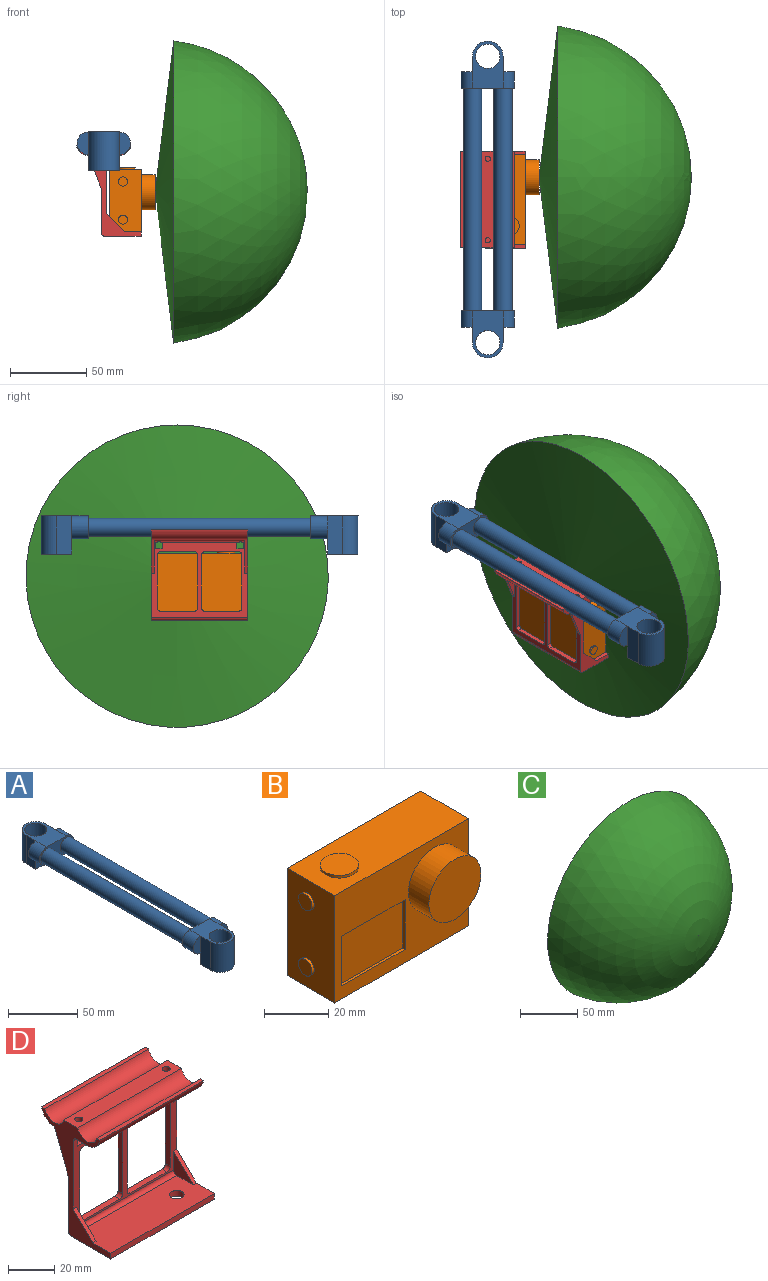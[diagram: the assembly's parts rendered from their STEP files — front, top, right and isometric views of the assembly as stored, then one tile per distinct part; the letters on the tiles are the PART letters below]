
ASSEMBLY  parts=4 mates=3
PART A: 28 faces, bbox 35x208x25 mm
  f0: plane 15x7.5mm, normal (0,1,0), area 88.4mm2, adj f11,f23
  f1: plane 15x7.5mm, normal (0,-1,0), area 88.4mm2, adj f7,f20
  f2: cylinder r=7.5mm len=15mm, axis (0,1,0), area 259.2mm2, adj f3,f4,f5,f6
  f3: plane 31x20mm, normal (0,0,1), area 376mm2, adj f2,f5,f7,f17,f18,f19,f20
  f4: plane 20x11mm, normal (0,0,-1), area 220mm2, adj f2,f5,f7,f16
  f5: plane 35x15mm, normal (0,1,0), area 250.5mm2, adj f2,f3,f4,f7,f8,f9
  f6: plane 15x7.5mm, normal (0,-1,0), area 88.4mm2, adj f2,f17
  f7: cylinder r=7.5mm len=15mm, axis (0,1,0), area 259.2mm2, adj f1,f3,f4,f5
  f8: cylinder r=6mm len=146mm, axis (0,1,0), area 5504.1mm2, adj f5,f10
  f9: cylinder r=6mm len=146mm, axis (0,1,0), area 5504.1mm2, adj f5,f10
  f10: plane 35x15mm, normal (0,-1,0), area 250.5mm2, adj f8,f9,f11,f12,f13,f14
  f11: cylinder r=7.5mm len=15mm, axis (0,-1,0), area 259.2mm2, adj f0,f10,f12,f13
  f12: plane 20x11mm, normal (0,0,-1), area 220mm2, adj f10,f11,f14,f22
  f13: plane 31x20mm, normal (0,0,1), area 376mm2, adj f10,f11,f14,f23,f24,f25,f26
  f14: cylinder r=7.5mm len=15mm, axis (0,-1,0), area 259.2mm2, adj f10,f12,f13,f15
  f15: plane 15x7.5mm, normal (0,1,0), area 88.4mm2, adj f14,f26
  f16: plane 20x10mm, normal (0,1,0), area 200mm2, adj f4,f17,f20,f21
  f17: plane 25x10mm, normal (-1,0,0), area 250mm2, adj f3,f6,f16,f18,f21
  f18: cylinder r=10mm len=25mm, axis (0,0,1), area 785.4mm2, adj f3,f17,f20,f21
  f19: cylinder r=8mm len=25mm, axis (0,0,1), area 1256.6mm2, adj f3,f21
  f20: plane 25x10mm, normal (1,0,0), area 250mm2, adj f1,f3,f16,f18,f21
  f21: plane 20x20mm, normal (0,0,-1), area 156mm2, adj f16,f17,f18,f19,f20
  f22: plane 20x10mm, normal (0,-1,0), area 200mm2, adj f12,f23,f26,f27
  f23: plane 25x10mm, normal (-1,0,0), area 250mm2, adj f0,f13,f22,f24,f27
  f24: cylinder r=10mm len=25mm, axis (0,0,1), area 785.4mm2, adj f13,f23,f26,f27
  f25: cylinder r=8mm len=25mm, axis (0,0,1), area 1256.6mm2, adj f13,f27
  f26: plane 25x10mm, normal (1,0,0), area 250mm2, adj f13,f15,f22,f24,f27
  f27: plane 20x20mm, normal (0,0,-1), area 156mm2, adj f22,f23,f24,f25,f26
PART B: 26 faces, bbox 60x30.1x42 mm
  f0: plane 41x21.1mm, normal (-1,0,0), area 808.6mm2, adj f1,f2,f3,f4,f5,f6
  f1: plane 59x21.1mm, normal (0,0,-1), area 1213.2mm2, adj f0,f2,f3,f7,f8
  f2: plane 59x41mm, normal (0,1,0), area 2419mm2, adj f0,f1,f4,f7
  f3: plane 59x41mm, normal (0,-1,0), area 1471.5mm2, adj f0,f1,f4,f7,f9,f10,f11,f12
  f4: plane 59x21.1mm, normal (0,0,1), area 1131.8mm2, adj f0,f2,f3,f7,f14
  f5: cylinder r=3mm len=6mm, axis (1,0,0), area 18.8mm2, adj f0,f15
  f6: cylinder r=3mm len=6mm, axis (1,0,0), area 18.8mm2, adj f0,f16
  f7: plane 41x21.1mm, normal (1,0,0), area 645.1mm2, adj f1,f2,f3,f4,f17,f18,f19,f20
  f8: cylinder r=3.17mm len=6.35mm, axis (0,0,-1), area 99.7mm2, adj f1,f21
  f9: plane 28x1mm, normal (0,0,-1), area 28mm2, adj f3,f10,f12,f22
  f10: plane 19x1mm, normal (1,0,0), area 19mm2, adj f3,f9,f11,f22
  f11: plane 28x1mm, normal (0,0,1), area 28mm2, adj f3,f10,f12,f22
  f12: plane 19x1mm, normal (-1,0,0), area 19mm2, adj f3,f9,f11,f22
  f13: cylinder r=11.5mm len=23mm, axis (0,1,0), area 650.3mm2, adj f3,f23
  f14: cylinder r=6mm len=12mm, axis (0,0,-1), area 37.7mm2, adj f4,f24
  f15: plane 6x6mm, normal (-1,0,0), area 28.3mm2, adj f5
  f16: plane 6x6mm, normal (-1,0,0), area 28.3mm2, adj f6
  f17: plane 22x1mm, normal (0,-1,0), area 22mm2, adj f7,f18,f20,f25
  f18: plane 10x1mm, normal (0,0,-1), area 10mm2, adj f7,f17,f19,f25
  f19: plane 22x1mm, normal (0,1,0), area 22mm2, adj f7,f18,f20,f25
  f20: plane 10x1mm, normal (0,0,1), area 10mm2, adj f7,f17,f19,f25
  f21: plane 6.35x6.35mm, normal (0,0,-1), area 31.7mm2, adj f8
  f22: plane 28x19mm, normal (0,-1,0), area 532mm2, adj f9,f10,f11,f12
  f23: plane 23x23mm, normal (0,-1,0), area 415.5mm2, adj f13
  f24: plane 12x12mm, normal (0,0,1), area 113.1mm2, adj f14
  f25: plane 22x10mm, normal (1,0,0), area 220mm2, adj f17,f18,f19,f20
PART C: 2 faces, bbox 198.5x100x198.5 mm
  f0: sphere r=100mm, area 55174.6mm2, adj f1
  f1: cone r=0mm half-angle=83deg, axis (0,-1,0), area 31181.8mm2, adj f0
PART D: 57 faces, bbox 63.5x42.4x59.5 mm
  f0: plane 63.5x46mm, normal (0,-1,0), area 784.9mm2, adj f3,f6,f18,f19,f22,f23,f26,f27
  f1: plane 63.5x49mm, normal (0,1,0), area 935.4mm2, adj f2,f13,f18,f19,f20,f21,f24,f25
  f2: cylinder r=2mm len=59.5mm, axis (-1,0,0), area 184mm2, adj f1,f7,f21,f25,f28,f29,f33,f34
  f3: cylinder r=2mm len=63.5mm, axis (-1,0,0), area 196.6mm2, adj f0,f10,f18,f19,f28,f29,f33,f34
  f4: plane 63.5x8.5mm, normal (0,0,1), area 520.5mm2, adj f16,f17,f18,f19,f28,f29
  f5: plane 63.5x21mm, normal (0,0,1), area 1261.8mm2, adj f6,f11,f18,f19,f22,f23,f26,f27
  f6: cylinder r=2mm len=59.5mm, axis (-1,0,0), area 186.9mm2, adj f0,f5,f23,f27
  f7: plane 59.5x6.5mm, normal (0,0,-1), area 386.8mm2, adj f2,f14,f21,f25
  f8: plane 63.5x2.05mm, normal (0,0,1), area 130.1mm2, adj f9,f17,f18,f19
  f9: cylinder r=8mm len=63.5mm, axis (-1,0,0), area 702.1mm2, adj f8,f10,f18,f19
  f10: plane 63.5x6.5mm, normal (0,0,-1), area 412.8mm2, adj f3,f9,f18,f19
  f11: plane 63.5x3mm, normal (0,-1,0), area 190.5mm2, adj f5,f12,f18,f19
  f12: plane 63.5x24mm, normal (0,0,-1), area 1492.3mm2, adj f11,f13,f18,f19,f40
  f13: cylinder r=2mm len=63.5mm, axis (-1,0,0), area 199.5mm2, adj f1,f12,f18,f19
  f14: cylinder r=8mm len=63.5mm, axis (-1,0,0), area 702.1mm2, adj f7,f15,f18,f19,f20,f24
  f15: plane 63.5x2.05mm, normal (0,0,1), area 130.1mm2, adj f14,f16,f18,f19
  f16: cylinder r=6mm len=63.5mm, axis (-1,0,0), area 990.3mm2, adj f4,f15,f18,f19
  f17: cylinder r=6mm len=63.5mm, axis (-1,0,0), area 990.3mm2, adj f4,f8,f18,f19
  f18: plane 59.5x42.36mm, normal (1,0,0), area 520.9mm2, adj f0,f1,f3,f4,f5,f8,f9,f10
  f19: plane 59.5x42.36mm, normal (-1,0,0), area 520.9mm2, adj f0,f1,f3,f4,f5,f8,f9,f10
  f20: plane 22x8.5mm, normal (0,0.93,-0.36), area 47.2mm2, adj f1,f14,f18,f21
  f21: plane 22x8.5mm, normal (-1,0,0), area 92.6mm2, adj f1,f2,f7,f20
  f22: plane 12x12mm, normal (0,-0.71,0.71), area 33.9mm2, adj f0,f5,f18,f23
  f23: plane 12x12mm, normal (-1,0,0), area 71.1mm2, adj f0,f5,f6,f22
  f24: plane 22x8.5mm, normal (0,0.93,-0.36), area 47.2mm2, adj f1,f14,f19,f25
  f25: plane 22x8.5mm, normal (1,0,0), area 92.6mm2, adj f1,f2,f7,f24
  f26: plane 12x12mm, normal (0,-0.71,0.71), area 33.9mm2, adj f0,f5,f19,f27
  f27: plane 12x12mm, normal (1,0,0), area 71.1mm2, adj f0,f5,f6,f26
  f28: cylinder r=1.75mm len=8.29mm, axis (0,0,1), area 88.2mm2, adj f2,f3,f4,f38,f39
  f29: cylinder r=1.75mm len=8.29mm, axis (0,0,1), area 88.2mm2, adj f2,f3,f4,f33,f34
  f30: plane 4.5x3mm, normal (0,0,1), area 13.5mm2, adj f0,f1,f31,f32
  f31: plane 4x3mm, normal (1,0,0), area 12mm2, adj f0,f1,f30,f33
  f32: plane 4x3mm, normal (-1,0,0), area 12mm2, adj f0,f1,f30,f34
  f33: plane 3x1.35mm, normal (0,0,-1), area 2.2mm2, adj f2,f3,f29,f31
  f34: plane 3x1.35mm, normal (0,0,-1), area 2.2mm2, adj f2,f3,f29,f32
  f35: plane 4.5x3mm, normal (0,0,1), area 13.5mm2, adj f0,f1,f36,f37
  f36: plane 4x3mm, normal (-1,0,0), area 12mm2, adj f0,f1,f35,f38
  f37: plane 4x3mm, normal (1,0,0), area 12mm2, adj f0,f1,f35,f39
  f38: plane 3x1.35mm, normal (0,0,-1), area 2.2mm2, adj f2,f3,f28,f36
  f39: plane 3x1.35mm, normal (0,0,-1), area 2.2mm2, adj f2,f3,f28,f37
  f40: cylinder r=3.17mm len=6.35mm, axis (0,0,-1), area 59.8mm2, adj f5,f12
  f41: plane 22.5x3mm, normal (0,0,-1), area 67.5mm2, adj f0,f1,f42,f48
  f42: cylinder r=2mm len=3mm, axis (0,1,0), area 9.4mm2, adj f0,f1,f41,f43
  f43: plane 35x3mm, normal (-1,0,0), area 105mm2, adj f0,f1,f42,f44
  f44: cylinder r=2mm len=3mm, axis (0,1,0), area 9.4mm2, adj f0,f1,f43,f45
  f45: plane 22.5x3mm, normal (0,0,1), area 67.5mm2, adj f0,f1,f44,f46
  f46: cylinder r=2mm len=3mm, axis (0,1,0), area 9.4mm2, adj f0,f1,f45,f47
  f47: plane 35x3mm, normal (1,0,0), area 105mm2, adj f0,f1,f46,f48
  f48: cylinder r=2mm len=3mm, axis (0,1,0), area 9.4mm2, adj f0,f1,f41,f47
  f49: plane 22.5x3mm, normal (0,0,-1), area 67.5mm2, adj f0,f1,f50,f56
  f50: cylinder r=2mm len=3mm, axis (0,1,0), area 9.4mm2, adj f0,f1,f49,f51
  f51: plane 35x3mm, normal (-1,0,0), area 105mm2, adj f0,f1,f50,f52
  f52: cylinder r=2mm len=3mm, axis (0,1,0), area 9.4mm2, adj f0,f1,f51,f53
  f53: plane 22.5x3mm, normal (0,0,1), area 67.5mm2, adj f0,f1,f52,f54
  f54: cylinder r=2mm len=3mm, axis (0,1,0), area 9.4mm2, adj f0,f1,f53,f55
  f55: plane 35x3mm, normal (1,0,0), area 105mm2, adj f0,f1,f54,f56
  f56: cylinder r=2mm len=3mm, axis (0,1,0), area 9.4mm2, adj f0,f1,f49,f55
PLACE A t=(-4.58,27.06,6.33)mm
PLACE B rot(axis=(0,0,1),90deg) t=(-0.98,27.31,-31.17)mm
PLACE C rot(axis=(-0.71,0.71,0),180deg) t=(82.3,41.81,-25.67)mm
PLACE D rot(axis=(0,0,1),90deg) t=(-4.58,27.06,-1.67)mm
MATE fastened C.f1 <-> B.f13  axis (1,0,0) through (29.12,41.81,-25.67)mm
MATE slider D.f9 <-> A.f9  axis (0,-1,0) through (5.42,27.06,6.33)mm
MATE fastened B.f8 <-> D.f40  axis (0,0,-1) through (9.02,46.61,-51.67)mm
